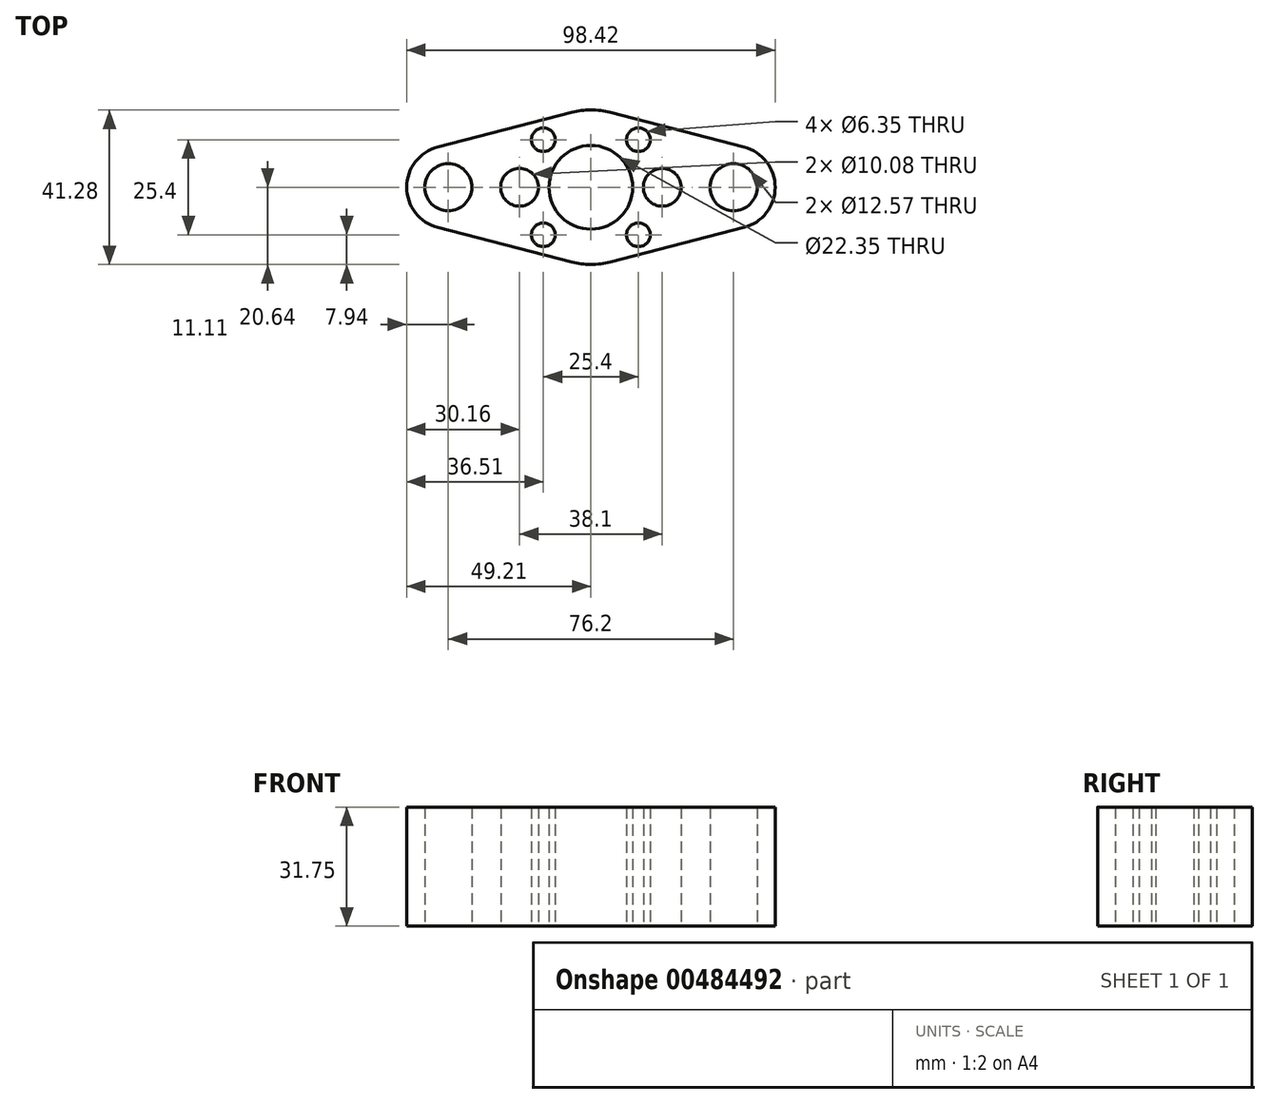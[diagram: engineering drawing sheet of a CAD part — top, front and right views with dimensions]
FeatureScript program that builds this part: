
annotation { "Feature Type Name" : "Feature", "Feature Type Description" : "" }
export const myFeature = defineFeature(function(context is Context, id is Id, definition is map)
    precondition{}
    {
        {
            var Q0;
            Q0=qCreatedBy(makeId("Top.planeOp"),FACE);
            var sketch = newSketch(context, id + "F0", { "sketchPlane" : qUnion([Q0])});
            skCircle(sketch, "E0", {"center": v(0, 0) * mm, "radius": 11.18 * mm});
            skCircle(sketch, "E1", {"center": v(-19.05, 0) * mm, "radius": 5.04 * mm});
            skCircle(sketch, "E2", {"center": v(19.05, 0) * mm, "radius": 5.04 * mm});
            skLineSegment(sketch, "E3", {"start": v(-19.05, 0) * mm, "end": v(19.05, 0) * mm, "construction": true});
            skCircle(sketch, "E4", {"center": v(-38.1, 0) * mm, "radius": 6.29 * mm});
            skCircle(sketch, "E5", {"center": v(38.1, 0) * mm, "radius": 6.29 * mm});
            skLineSegment(sketch, "E6", {"start": v(-19.05, 0) * mm, "end": v(-38.1, 0) * mm, "construction": true});
            skLineSegment(sketch, "E7", {"start": v(19.05, 0) * mm, "end": v(38.1, 0) * mm, "construction": true});
            skArc(sketch, "E8", {"start": v(-40.88, 10.76) * mm, "mid": v(-49.21, 0) * mm, "end": v(-40.88, -10.76) * mm});
            skArc(sketch, "E9", {"start": v(40.88, -10.76) * mm, "mid": v(49.21, 0) * mm, "end": v(40.88, 10.76) * mm});
            skArc(sketch, "E10", {"start": v(-5.16, -19.98) * mm, "mid": v(0, -20.64) * mm, "end": v(5.16, -19.98) * mm});
            skLineSegment(sketch, "E11", {"start": v(-40.88, 10.76) * mm, "end": v(-5.16, 19.98) * mm});
            skLineSegment(sketch, "E12", {"start": v(5.16, 19.98) * mm, "end": v(40.88, 10.76) * mm});
            skLineSegment(sketch, "E13", {"start": v(-40.88, -10.76) * mm, "end": v(-5.16, -19.98) * mm});
            skLineSegment(sketch, "E14", {"start": v(5.16, -19.98) * mm, "end": v(40.88, -10.76) * mm});
            skArc(sketch, "E15.trimOffspring", {"start": v(5.16, 19.98) * mm, "mid": v(0, 20.64) * mm, "end": v(-5.16, 19.98) * mm});
            skLineSegment(sketch, "E16.bottom", {"start": v(-12.7, 12.7) * mm, "end": v(12.7, 12.7) * mm, "construction": true});
            skLineSegment(sketch, "E16.top", {"start": v(-12.7, -12.7) * mm, "end": v(12.7, -12.7) * mm, "construction": true});
            skLineSegment(sketch, "E16.left", {"start": v(-12.7, 12.7) * mm, "end": v(-12.7, -12.7) * mm, "construction": true});
            skLineSegment(sketch, "E16.right", {"start": v(12.7, 12.7) * mm, "end": v(12.7, -12.7) * mm, "construction": true});
            skCircle(sketch, "E17", {"center": v(-12.7, 12.7) * mm, "radius": 3.18 * mm});
            skCircle(sketch, "E18", {"center": v(-12.7, -12.7) * mm, "radius": 3.18 * mm});
            skCircle(sketch, "E19", {"center": v(12.7, -12.7) * mm, "radius": 3.18 * mm});
            skCircle(sketch, "E20", {"center": v(12.7, 12.7) * mm, "radius": 3.18 * mm});
            skSolve(sketch);
        }
        {
            var Q0;
            Q0=qSketchRegion(id+"F0",true);
            extrude(context, id + "F1", {"entities" : qUnion([Q0]), "depth" : 31.75 * mm});
        }
    });
